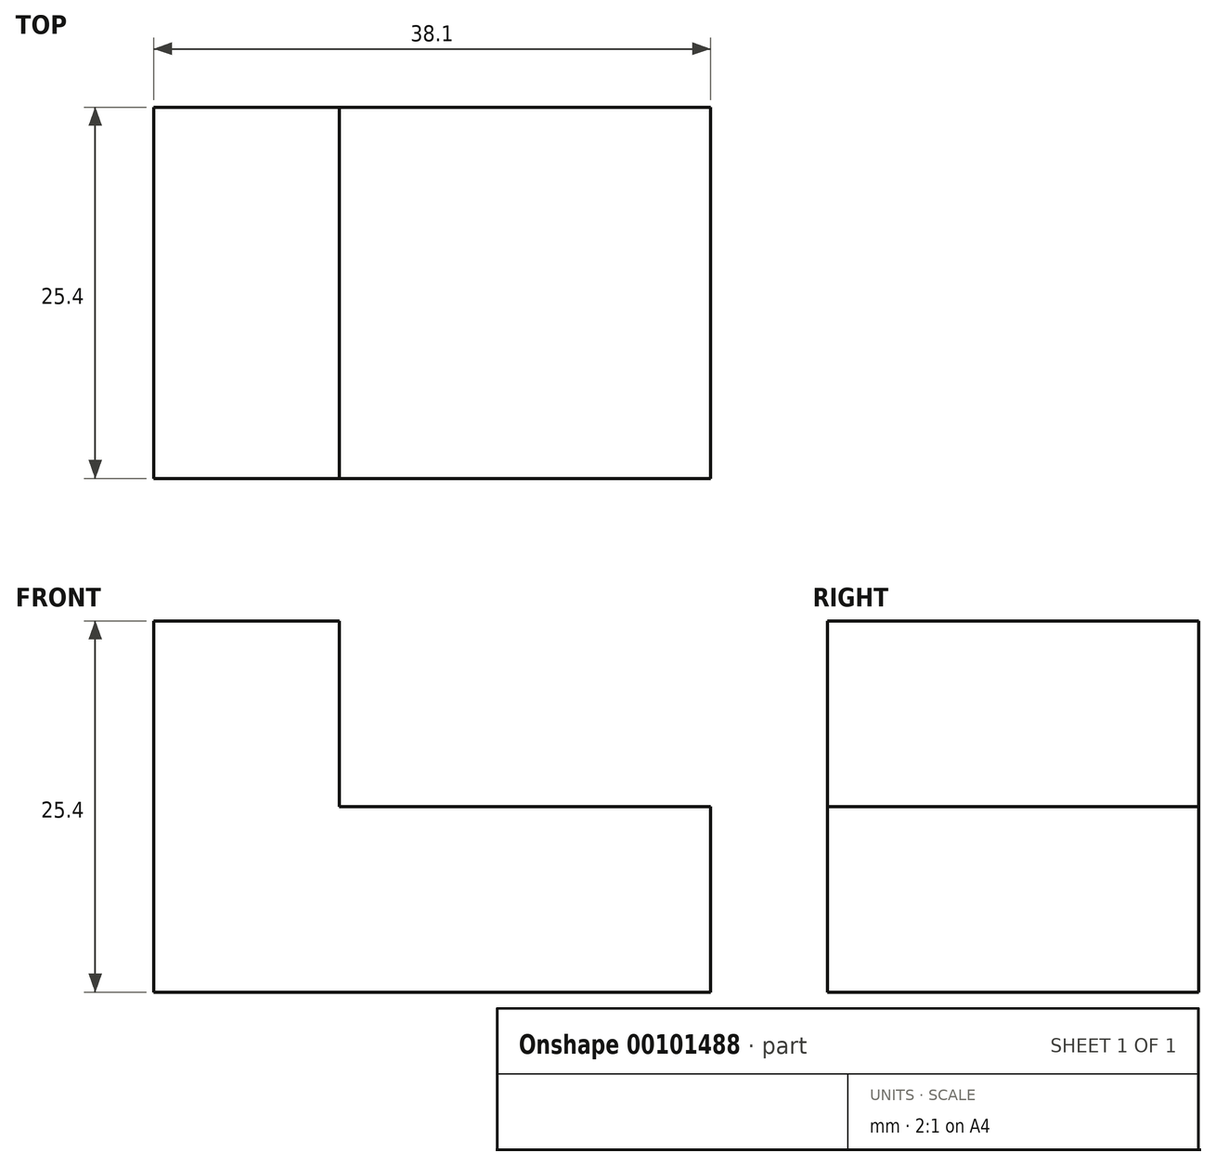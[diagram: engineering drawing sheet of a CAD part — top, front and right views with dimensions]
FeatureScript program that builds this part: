
annotation { "Feature Type Name" : "Feature", "Feature Type Description" : "" }
export const myFeature = defineFeature(function(context is Context, id is Id, definition is map)
    precondition{}
    {
        {
            var Q0;
            Q0=qCreatedBy(makeId("Front.planeOp"),FACE);
            var sketch = newSketch(context, id + "F0", { "sketchPlane" : qUnion([Q0])});
            skLineSegment(sketch, "E0", {"start": v(0, 0) * mm, "end": v(38.1, 0) * mm});
            skLineSegment(sketch, "E1", {"start": v(38.1, 0) * mm, "end": v(38.1, 12.7) * mm});
            skLineSegment(sketch, "E2", {"start": v(38.1, 12.7) * mm, "end": v(12.7, 12.7) * mm});
            skLineSegment(sketch, "E3", {"start": v(12.7, 12.7) * mm, "end": v(12.7, 25.4) * mm});
            skLineSegment(sketch, "E4", {"start": v(12.7, 25.4) * mm, "end": v(0, 25.4) * mm});
            skLineSegment(sketch, "E5", {"start": v(0, 25.4) * mm, "end": v(0, 0) * mm});
            skSolve(sketch);
        }
        {
            var Q0;
            Q0=makeQuery(id+"F0.imprint","IMPRINT",FACE,{"disambiguationData":[TD([[makeQuery(id+"F0.imprint","IMPRINT",EDGE,{"derivedFrom":sQuery(id+"F0.wireOp",EDGE,"E0")}),1.0]])]});
            extrude(context, id + "F1", {"entities" : qUnion([Q0]), "depth" : 25.4 * mm});
        }
    });
